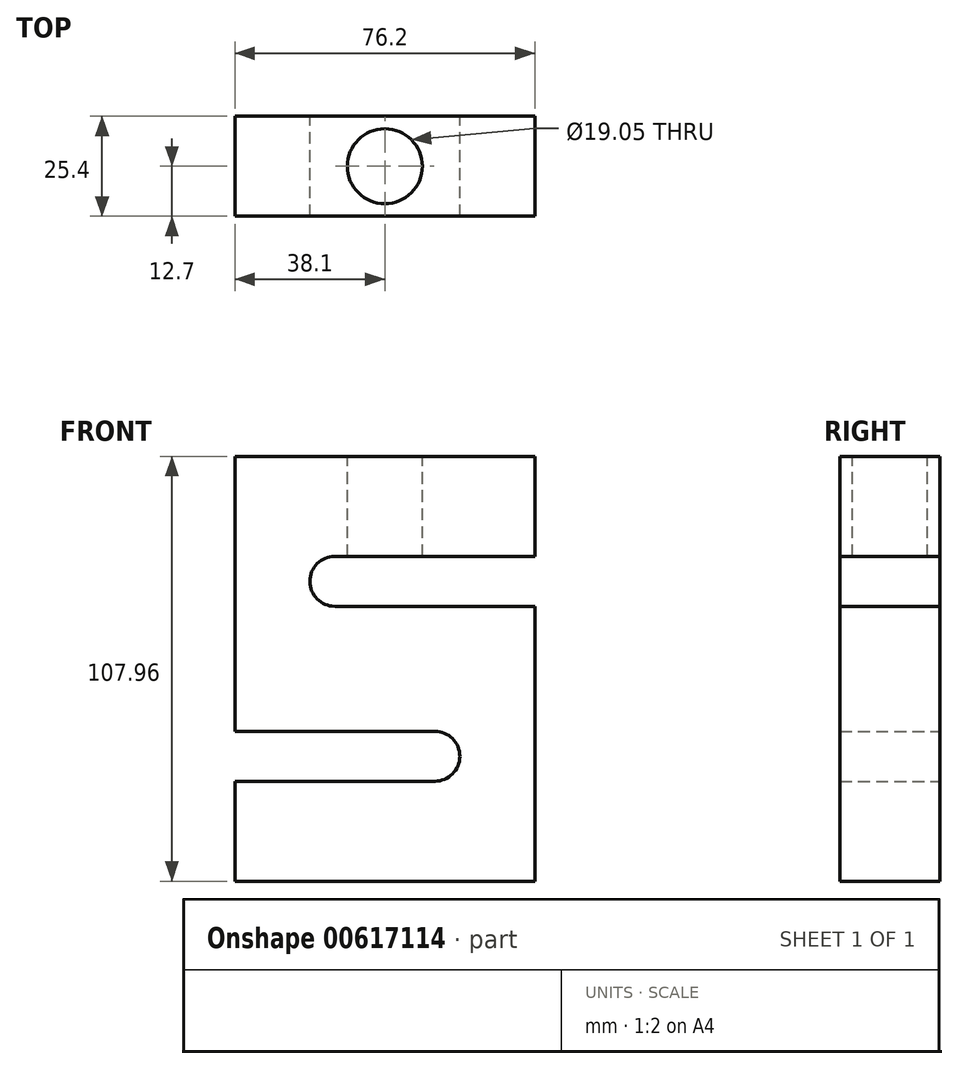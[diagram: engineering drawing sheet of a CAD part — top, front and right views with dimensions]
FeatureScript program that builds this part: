
annotation { "Feature Type Name" : "Feature", "Feature Type Description" : "" }
export const myFeature = defineFeature(function(context is Context, id is Id, definition is map)
    precondition{}
    {
        {
            var Q0;
            Q0=qCreatedBy(makeId("Front.planeOp"),FACE);
            var sketch = newSketch(context, id + "F0", { "sketchPlane" : qUnion([Q0])});
            skLineSegment(sketch, "E0.bottom", {"start": v(-38.1, 53.98) * mm, "end": v(38.1, 53.98) * mm});
            skLineSegment(sketch, "E0.top", {"start": v(-38.1, -53.98) * mm, "end": v(38.1, -53.98) * mm});
            skLineSegment(sketch, "E0.left", {"start": v(-38.1, 53.98) * mm, "end": v(-38.1, -15.87) * mm});
            skLineSegment(sketch, "E0.right", {"start": v(38.1, 53.98) * mm, "end": v(38.1, 28.57) * mm});
            skLineSegment(sketch, "E1.bottom", {"start": v(-38.1, -15.87) * mm, "end": v(12.7, -15.87) * mm});
            skLineSegment(sketch, "E1.top", {"start": v(-38.1, -28.57) * mm, "end": v(12.7, -28.57) * mm});
            skLineSegment(sketch, "E2.trimOffspring", {"start": v(-38.1, -28.57) * mm, "end": v(-38.1, -53.98) * mm});
            skLineSegment(sketch, "E3.bottom", {"start": v(38.1, 28.57) * mm, "end": v(-12.7, 28.57) * mm});
            skLineSegment(sketch, "E3.top", {"start": v(38.1, 15.87) * mm, "end": v(-12.7, 15.87) * mm});
            skLineSegment(sketch, "E4.trimOffspring", {"start": v(38.1, 15.87) * mm, "end": v(38.1, -53.98) * mm});
            skArc(sketch, "E5", {"start": v(-12.7, 28.57) * mm, "mid": v(-19.05, 22.22) * mm, "end": v(-12.7, 15.87) * mm});
            skArc(sketch, "E6", {"start": v(12.7, -28.57) * mm, "mid": v(19.05, -22.22) * mm, "end": v(12.7, -15.87) * mm});
            skLineSegment(sketch, "E7", {"start": v(0, 53.98) * mm, "end": v(0, 0) * mm, "construction": true});
            skLineSegment(sketch, "E8", {"start": v(0, 0) * mm, "end": v(0, -53.98) * mm, "construction": true});
            skSolve(sketch);
        }
        {
            var Q0;
            Q0 = qSketchRegion(id + "F0", true);
            extrude(context, id + "F1", {"entities" : qUnion([Q0]), "depth" : 25.4 * mm, "offsetDistance" : 25.4 * mm});
        }
        {
            var Q0;
            Q0=makeQuery(id+"F1.opExtrude","SWEPT_FACE",FACE,{"disambiguationData":[OSD([sQuery(id+"F0.wireOp",EDGE,"E0.bottom")])]});
            var sketch = newSketch(context, id + "F2", { "sketchPlane" : qUnion([Q0])});
            skCircle(sketch, "E9", {"center": v(0, -12.7) * mm, "radius": 9.52 * mm});
            skLineSegment(sketch, "E10", {"start": v(-38.1, -12.7) * mm, "end": v(38.1, -12.7) * mm, "construction": true});
            skLineSegment(sketch, "E11", {"start": v(0, -25.4) * mm, "end": v(0, 0) * mm, "construction": true});
            skSolve(sketch);
        }
        {
            var Q0;
            Q0 = qSketchRegion(id + "F2", true);
            extrude(context, id + "F3", {"entities" : qUnion([Q0]), "operationType" : NewBodyOperationType.REMOVE, "endBound" : BoundingType.UP_TO_NEXT, "oppositeDirection" : true, "depth" : 25.4 * mm, "offsetDistance" : 25.4 * mm});
        }
    });
